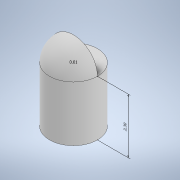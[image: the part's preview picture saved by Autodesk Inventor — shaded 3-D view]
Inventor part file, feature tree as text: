
AUTODESK INVENTOR PART (.ipt)
format: ipt  version: 2020 (Build 240168000, 168)  size: 123,392 bytes
history: native  units: mm
features: other x2, revolve x2, sketch x2
ambient origin geometry x8: Origin, YZ Plane, XZ Plane, XY Plane, X Axis, Y Axis, Z Axis, Center Point
bodies: Solid1 (feature_tree)
feature tree (6):
  other  "Annotations"
  revolve  "Revolution1"  [1 undecoded]
  sketch  "Sketch2"  dims[d5=90.0deg d10=2.3mm]
  revolve  "Revolution3"  [1 undecoded]
  sketch  "Sketch4"  dims[d11=1.0mm d12=1.0mm d13=180.0deg d14=0.01mm d15=2.3mm]
  other  "Linear Dimension 1"
note: 2 required parameter values undecoded (feature->parameter linkage not recoverable at this tier; creation-order binding heuristic only, values carry confidence <= 0.55)
